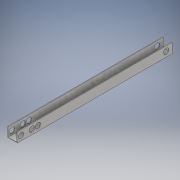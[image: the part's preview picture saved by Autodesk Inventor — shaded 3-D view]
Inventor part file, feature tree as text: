
AUTODESK INVENTOR PART (.ipt)
format: ipt  version: 2018 (Build 220112000, 112)  size: 136,192 bytes
history: native  units: in
note: dims shown in document units (in); Inventor stores cm internally (conversion verified against a paired STEP export)
features: extrude x4, sketch x4
ambient origin geometry x8: Origin, YZ Plane, XZ Plane, XY Plane, X Axis, Y Axis, Z Axis, Center Point
bodies: Solid1 (feature_tree)
feature tree (8):
  extrude  "Extrusion1"  Depth=32.0in
  extrude  "Extrusion2"  Depth=0.125in
  extrude  "Extrusion3"  Depth=1.75in
  extrude  "Extrusion4"  Depth=1.875in TaperAngle=0.0deg
  sketch  "Sketch1"  dims[d0=2.0in d1=32.0in]
  sketch  "Sketch2"  dims[d2=2.0in d3=0.0in d4=0.125in]
  sketch  "Sketch3"  dims[d5=0.125in d6=1.75in]
  sketch  "Sketch4"  dims[d7=32.0in d8=1.875in d9=0.0in d10=0.75in d11=1.125in d12=2.25in d13=1.125in d14=1.25in d15=1.125in d16=3.0in d17=0.0in d18=1.25in d19=1.125in d20=3.0in d21=0.0in]
